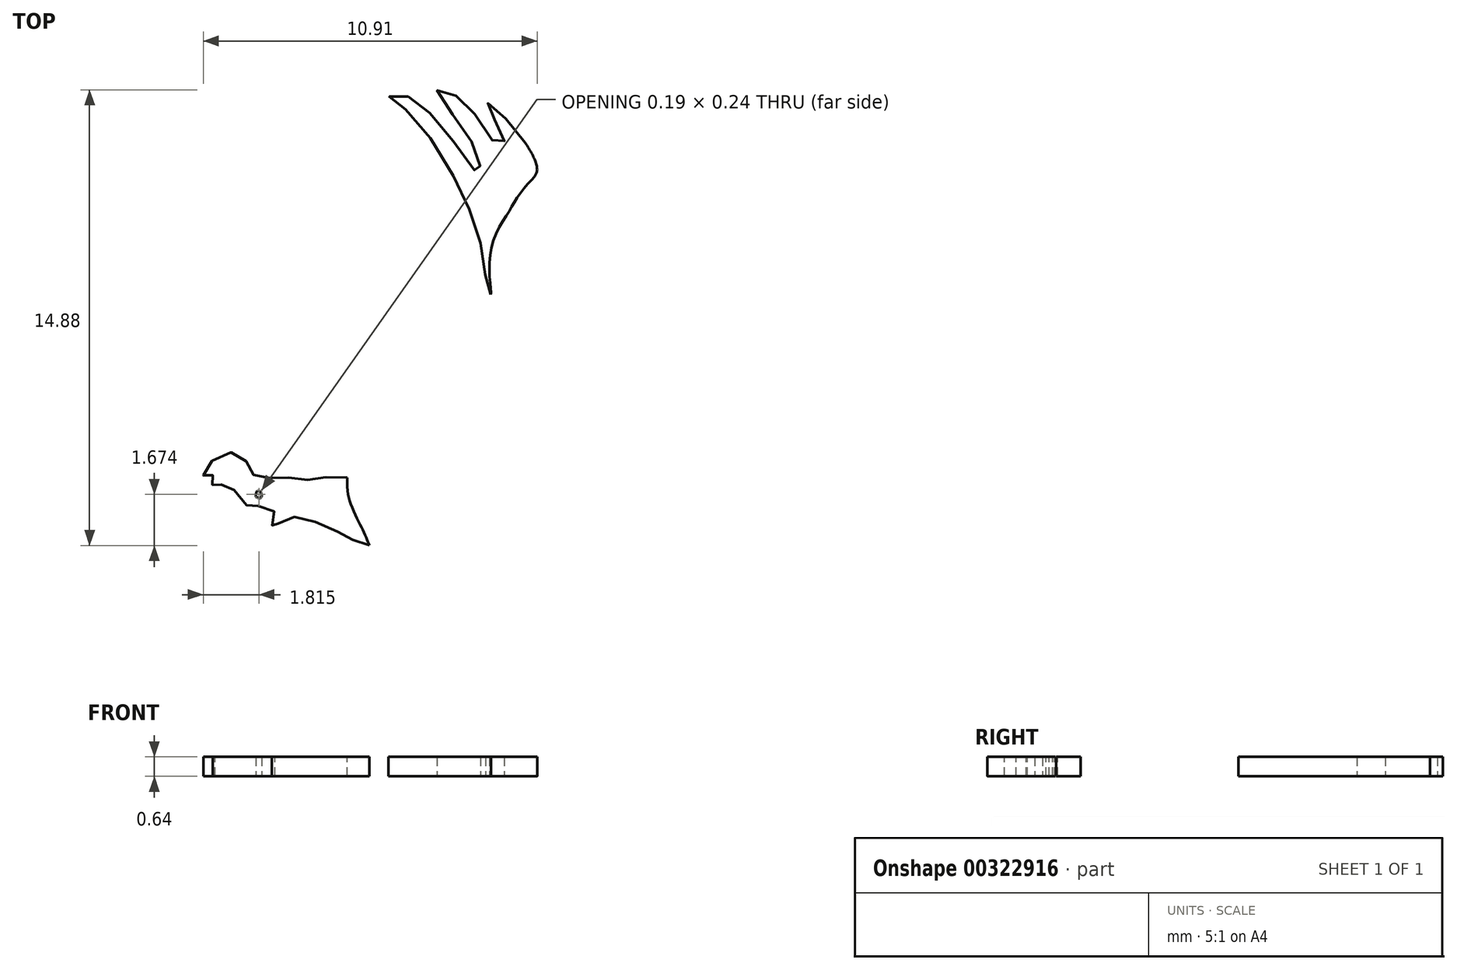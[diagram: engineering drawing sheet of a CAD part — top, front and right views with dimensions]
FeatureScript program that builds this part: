
annotation { "Feature Type Name" : "Feature", "Feature Type Description" : "" }
export const myFeature = defineFeature(function(context is Context, id is Id, definition is map)
    precondition{}
    {
        {
            var Q0;
            Q0=qCreatedBy(makeId("Top.planeOp"),FACE);
            var sketch = newSketch(context, id + "F0", { "sketchPlane" : qUnion([Q0])});
            skLineSegment(sketch, "E0", {"start": v(-2.65, -7.8) * mm, "end": v(0.66, -7.8) * mm});
            skLineSegment(sketch, "E1", {"start": v(0.66, -7.8) * mm, "end": v(-0.1, -6.67) * mm});
            skLineSegment(sketch, "E2", {"start": v(-0.1, -6.67) * mm, "end": v(-3.36, -6.67) * mm});
            skLineSegment(sketch, "E3", {"start": v(-3.36, -6.67) * mm, "end": v(-2.65, -7.8) * mm});
            skLineSegment(sketch, "E4", {"start": v(4.6, -7.8) * mm, "end": v(7.37, -7.7) * mm});
            skLineSegment(sketch, "E5", {"start": v(7.37, -7.7) * mm, "end": v(6.5, -6.65) * mm});
            skLineSegment(sketch, "E6", {"start": v(6.5, -6.65) * mm, "end": v(3.6, -6.73) * mm});
            skLineSegment(sketch, "E7", {"start": v(3.6, -6.73) * mm, "end": v(4.6, -7.8) * mm});
            skFitSpline(sketch, "E8", {"points": [v(-7.27, -6.68) * mm, v(-7.08, -6.58) * mm, v(-6.94, -6.5) * mm, v(-6.73, -6.5) * mm, v(-6.69, -6.62) * mm, v(-6.5, -6.89) * mm, v(-6.2, -7.32) * mm, v(-6.03, -7.65) * mm, v(-6.02, -7.73) * mm, v(-6, -7.8) * mm, v(-6.35, -7.85) * mm, v(-6.98, -7.9) * mm, v(-7.9, -7.87) * mm, v(-8.38, -7.71) * mm, v(-8.62, -7.55) * mm, v(-8.68, -7.37) * mm, v(-8.61, -7.07) * mm, v(-8.44, -6.87) * mm, v(-7.98, -6.7) * mm, v(-7.53, -6.56) * mm, v(-7.4, -6.48) * mm, v(-7.36, -6.46) * mm, v(-7.32, -6.52) * mm, v(-7.3, -6.6) * mm, v(-7.27, -6.68) * mm]});
            skFitSpline(sketch, "E9", {"points": [v(-1.27, -6.52) * mm, v(-1.14, -6.29) * mm, v(-1.06, -6.05) * mm, v(-1.05, -5.83) * mm, v(-1.06, -5.78) * mm, v(-1.19, -5.86) * mm, v(-1.37, -6.07) * mm, v(-1.44, -6.33) * mm, v(-1.43, -6.42) * mm, v(-1.35, -6.5) * mm, v(-1.27, -6.52) * mm]});
            skFitSpline(sketch, "E10", {"points": [v(8, -5.7) * mm, v(8.08, -5.77) * mm, v(8.1, -5.98) * mm, v(7.99, -6.24) * mm, v(7.85, -6.36) * mm, v(7.79, -6.4) * mm, v(7.71, -6.31) * mm, v(7.7, -6.05) * mm, v(7.85, -5.82) * mm, v(8, -5.7) * mm]});
            skFitSpline(sketch, "E11", {"points": [v(-2.87, -2.94) * mm, v(-2.6, -2.91) * mm, v(-2.31, -2.71) * mm, v(-2.17, -2.46) * mm, v(-2.17, -2.41) * mm, v(-2.24, -2.33) * mm, v(-2.33, -2.3) * mm, v(-2.48, -2.4) * mm, v(-2.62, -2.58) * mm, v(-2.74, -2.76) * mm, v(-2.8, -2.86) * mm, v(-2.87, -2.94) * mm]});
            skFitSpline(sketch, "E12", {"points": [v(-3.18, 5.99) * mm, v(-3.22, 6.13) * mm, v(-3.35, 6.22) * mm, v(-3.54, 6.2) * mm, v(-3.64, 6.1) * mm, v(-3.64, 5.97) * mm, v(-3.5, 5.88) * mm, v(-3.27, 5.92) * mm, v(-3.2, 5.95) * mm, v(-3.18, 5.99) * mm]});
            skFitSpline(sketch, "E13", {"points": [v(-8.53, -0.56) * mm, v(-8.5, -0.45) * mm, v(-8.54, -0.37) * mm, v(-8.61, -0.32) * mm, v(-8.67, -0.37) * mm, v(-8.7, -0.46) * mm, v(-8.7, -0.51) * mm, v(-8.63, -0.57) * mm, v(-8.53, -0.56) * mm]});
            skFitSpline(sketch, "E14", {"points": [v(-5.7, 0.1) * mm, v(-5.7, -0.28) * mm, v(-5.62, -0.68) * mm, v(-5.41, -1.2) * mm, v(-5.23, -1.54) * mm, v(-5.1, -1.8) * mm, v(-5.03, -2) * mm, v(-4.99, -2.11) * mm, v(-5.11, -2.1) * mm, v(-5.51, -1.95) * mm, v(-5.6, -1.88) * mm, v(-5.87, -1.74) * mm, v(-6.4, -1.5) * mm, v(-6.88, -1.3) * mm, v(-7.3, -1.2) * mm, v(-7.67, -1.22) * mm, v(-7.92, -1.35) * mm, v(-8.05, -1.5) * mm, v(-8.11, -1.57) * mm, v(-8.14, -1.55) * mm, v(-8.16, -1.39) * mm, v(-8.09, -1.23) * mm, v(-8.1, -1) * mm, v(-8.27, -0.87) * mm, v(-8.63, -0.82) * mm, v(-8.84, -0.84) * mm, v(-8.94, -0.86) * mm, v(-9.03, -0.77) * mm, v(-9.27, -0.47) * mm, v(-9.48, -0.2) * mm, v(-9.63, -0.1) * mm, v(-9.85, -0.14) * mm, v(-10, -0.2) * mm, v(-10.07, -0.2) * mm, v(-10.1, -0.17) * mm, v(-10.08, -0.07) * mm, v(-10.03, 0.04) * mm, v(-10.06, 0.13) * mm, v(-10.13, 0.18) * mm, v(-10.23, 0.17) * mm, v(-10.35, 0.16) * mm, v(-10.4, 0.16) * mm, v(-10.33, 0.39) * mm, v(-10.17, 0.6) * mm, v(-9.85, 0.84) * mm, v(-9.44, 0.92) * mm, v(-9.13, 0.8) * mm, v(-8.97, 0.55) * mm, v(-8.87, 0.31) * mm, v(-8.76, 0.18) * mm, v(-8.6, 0.1) * mm, v(-8.3, 0.08) * mm, v(-7.91, 0.11) * mm, v(-7.6, 0.1) * mm, v(-7.2, 0) * mm, v(-6.9, 0.05) * mm, v(-6.58, 0.1) * mm, v(-6.17, 0.12) * mm, v(-5.7, 0.1) * mm, v(-5.7, 0.1) * mm]});
            skFitSpline(sketch, "E15", {"points": [v(-4.83, -5.9) * mm, v(-4.95, -5.73) * mm, v(-5.1, -5.65) * mm, v(-5.3, -5.65) * mm, v(-5.54, -5.76) * mm, v(-5.79, -5.98) * mm, v(-5.92, -6.16) * mm, v(-5.97, -6.24) * mm, v(-5.98, -6.28) * mm, v(-5.55, -6.31) * mm, v(-4.77, -6.33) * mm, v(-3.69, -6.33) * mm, v(-2.83, -6.32) * mm, v(-2.13, -6.33) * mm, v(-2, -6.32) * mm, v(-1.95, -6.3) * mm, v(-1.86, -6.05) * mm, v(-1.85, -6) * mm, v(-1.56, -5.66) * mm, v(-0.98, -5.46) * mm, v(-0.5, -5.44) * mm, v(-0.27, -5.46) * mm, v(-0.2, -5.42) * mm, v(0.38, -4.7) * mm, v(0.7, -4.3) * mm, v(0.85, -4.1) * mm, v(0.85, -3.83) * mm, v(0.82, -3.33) * mm, v(0.72, -2.88) * mm, v(0.67, -2.31) * mm, v(0.67, -2.17) * mm, v(0.6, -2.14) * mm, v(0.54, -2.07) * mm, v(0.45, -2.1) * mm, v(0.04, -2.3) * mm, v(-0.47, -2.54) * mm, v(-1.24, -2.9) * mm, v(-1.8, -3.06) * mm, v(-2.52, -3.16) * mm, v(-2.97, -3.26) * mm, v(-3.3, -3.4) * mm, v(-3.71, -3.86) * mm, v(-4, -4.26) * mm, v(-4.05, -4.32) * mm, v(-4.4, -4.69) * mm, v(-4.59, -4.91) * mm, v(-4.77, -5.3) * mm, v(-4.81, -5.63) * mm, v(-4.82, -5.85) * mm, v(-4.83, -5.9) * mm]});
            skFitSpline(sketch, "E16", {"points": [v(8.37, -5.29) * mm, v(8.16, -4.77) * mm, v(7.88, -4.27) * mm, v(7.55, -3.92) * mm, v(7.26, -3.8) * mm, v(6.8, -3.76) * mm, v(6.22, -3.8) * mm, v(5.74, -3.85) * mm, v(5.47, -3.84) * mm, v(5.3, -3.83) * mm, v(5.2, -3.83) * mm, v(4.99, -3.42) * mm, v(4.73, -2.73) * mm, v(4.57, -2.26) * mm, v(4.38, -1.86) * mm, v(4.22, -1.6) * mm, v(4.16, -1.51) * mm, v(3.83, -1.45) * mm, v(3.42, -1.35) * mm, v(3.05, -1.34) * mm, v(2.72, -1.62) * mm, v(2.49, -2.08) * mm, v(2.43, -2.92) * mm, v(2.45, -4) * mm, v(2.44, -4.4) * mm, v(2.44, -4.48) * mm, v(2.2, -4.6) * mm, v(1.84, -4.83) * mm, v(1.04, -5.37) * mm, v(0.61, -5.65) * mm, v(0.32, -5.9) * mm, v(0.08, -6.2) * mm, v(0.04, -6.27) * mm, v(0.38, -6.3) * mm, v(2.63, -6.34) * mm, v(4.92, -6.32) * mm, v(6.38, -6.3) * mm, v(6.85, -6.28) * mm, v(7, -6.28) * mm, v(7.04, -6.18) * mm, v(7.24, -5.82) * mm, v(7.73, -5.45) * mm, v(8.14, -5.34) * mm, v(8.4, -5.33) * mm, v(8.37, -5.29) * mm]});
            skFitSpline(sketch, "E17", {"points": [v(-1.02, 6.22) * mm, v(-1.06, 6.93) * mm, v(-0.88, 7.98) * mm, v(-0.45, 8.75) * mm, v(-0.18, 9.2) * mm, v(0.21, 9.7) * mm, v(0.48, 10.05) * mm, v(0.44, 10.42) * mm, v(0.1, 11.04) * mm, v(-0.33, 11.6) * mm, v(-0.67, 11.98) * mm, v(-0.98, 12.24) * mm, v(-1.17, 12.34) * mm, v(-1.18, 12.24) * mm, v(-0.9, 11.79) * mm, v(-0.71, 11.5) * mm, v(-0.57, 11.08) * mm, v(-0.62, 10.88) * mm, v(-0.8, 10.94) * mm, v(-1.24, 11.48) * mm, v(-1.57, 12) * mm, v(-1.87, 12.35) * mm, v(-2.27, 12.63) * mm, v(-2.63, 12.74) * mm, v(-2.77, 12.75) * mm, v(-2.66, 12.51) * mm, v(-2.2, 11.88) * mm, v(-1.75, 11.28) * mm, v(-1.43, 10.6) * mm, v(-1.37, 10.3) * mm, v(-1.36, 10.09) * mm, v(-1.36, 9.95) * mm, v(-1.7, 10.33) * mm, v(-2.21, 11.04) * mm, v(-2.84, 11.82) * mm, v(-3.35, 12.3) * mm, v(-3.71, 12.53) * mm, v(-3.76, 12.56) * mm, v(-4.17, 12.57) * mm, v(-4.34, 12.53) * mm, v(-4.36, 12.48) * mm, v(-4.08, 12.33) * mm, v(-3.39, 11.7) * mm, v(-2.77, 10.85) * mm, v(-2.08, 9.65) * mm, v(-1.71, 8.84) * mm, v(-1.42, 7.98) * mm, v(-1.25, 7.28) * mm, v(-1.2, 6.6) * mm, v(-1.17, 6.3) * mm, v(-1.03, 6.08) * mm, v(-1.02, 6.22) * mm]});
            skFitSpline(sketch, "E18", {"points": [v(-7.76, -6.35) * mm, v(-7.74, -6.2) * mm, v(-7.65, -5.96) * mm, v(-7.41, -5.68) * mm, v(-7.15, -5.53) * mm, v(-6.75, -5.42) * mm, v(-6.4, -5.39) * mm, v(-6.23, -5.4) * mm, v(-6.04, -5.12) * mm, v(-5.68, -4.5) * mm, v(-5.3, -3.77) * mm, v(-4.76, -2.73) * mm, v(-4.63, -2.49) * mm, v(-4.61, -2.45) * mm, v(-4.6, -2.43) * mm, v(-4.63, -2.33) * mm, v(-4.73, -2.1) * mm, v(-4.87, -1.8) * mm, v(-4.9, -1.72) * mm, v(-4.9, -1.51) * mm, v(-4.88, -1.26) * mm, v(-4.82, -0.87) * mm, v(-4.72, -0.49) * mm, v(-4.59, -0.09) * mm, v(-4.4, 0.34) * mm, v(-4.34, 0.49) * mm, v(-4.32, 0.52) * mm, v(-4.16, 0.66) * mm, v(-4.07, 0.8) * mm, v(-4.06, 0.95) * mm, v(-4.09, 1.04) * mm, v(-4.15, 1.03) * mm, v(-4.37, 0.9) * mm, v(-4.53, 0.75) * mm, v(-4.73, 0.45) * mm, v(-4.86, 0.17) * mm, v(-4.97, -0.22) * mm, v(-5.02, -0.63) * mm, v(-5.04, -0.96) * mm, v(-5.04, -1.1) * mm, v(-5.03, -1.12) * mm, v(-5.1, -1.05) * mm, v(-5.3, -0.68) * mm, v(-5.45, -0.18) * mm, v(-5.5, 0.17) * mm, v(-5.52, 0.6) * mm, v(-5.46, 1.1) * mm, v(-5.36, 1.5) * mm, v(-5.08, 2.18) * mm, v(-4.6, 2.97) * mm, v(-4.11, 3.6) * mm, v(-3.9, 3.83) * mm, v(-3.72, 3.93) * mm, v(-3.5, 4.12) * mm, v(-3.43, 4.24) * mm, v(-3.42, 4.33) * mm, v(-3.45, 4.43) * mm, v(-3.54, 4.47) * mm, v(-3.78, 4.4) * mm, v(-4.07, 4.17) * mm, v(-4.35, 3.98) * mm, v(-4.54, 3.9) * mm, v(-4.64, 3.86) * mm, v(-4.7, 3.86) * mm, v(-4.72, 3.86) * mm, v(-4.72, 3.92) * mm, v(-4.55, 4.11) * mm, v(-4.27, 4.3) * mm, v(-4.09, 4.48) * mm, v(-4.02, 4.65) * mm, v(-4, 4.73) * mm, v(-4.07, 4.74) * mm, v(-4.27, 4.77) * mm, v(-4.47, 4.73) * mm, v(-4.64, 4.64) * mm, v(-4.82, 4.45) * mm, v(-5, 4.2) * mm, v(-5.18, 3.92) * mm, v(-5.35, 3.7) * mm, v(-5.54, 3.54) * mm, v(-5.68, 3.47) * mm, v(-5.84, 3.47) * mm, v(-6.04, 3.45) * mm, v(-6.2, 3.4) * mm, v(-6.27, 3.32) * mm, v(-6.3, 3.28) * mm, v(-6.33, 3.28) * mm, v(-6.46, 3.4) * mm, v(-6.6, 3.57) * mm, v(-6.7, 3.78) * mm, v(-6.76, 3.9) * mm, v(-6.76, 3.92) * mm, v(-6.64, 3.94) * mm, v(-6.63, 3.94) * mm, v(-6.4, 4) * mm, v(-6.19, 4.04) * mm, v(-5.99, 4.06) * mm, v(-6, 3.98) * mm, v(-6.11, 3.88) * mm, v(-6.16, 3.83) * mm, v(-6.16, 3.78) * mm, v(-6.06, 3.73) * mm, v(-5.88, 3.68) * mm, v(-5.68, 3.72) * mm, v(-5.47, 3.85) * mm, v(-5.29, 4.04) * mm, v(-5.03, 4.37) * mm, v(-4.84, 4.6) * mm, v(-4.65, 4.8) * mm, v(-4.52, 4.92) * mm, v(-4.35, 5) * mm, v(-4.18, 5) * mm, v(-4.05, 4.98) * mm, v(-3.9, 4.91) * mm, v(-3.77, 4.82) * mm, v(-3.75, 4.8) * mm, v(-3.72, 4.78) * mm, v(-3.62, 4.9) * mm, v(-3.54, 5.03) * mm, v(-3.53, 5.2) * mm, v(-3.55, 5.3) * mm, v(-3.66, 5.34) * mm, v(-3.98, 5.4) * mm, v(-4.28, 5.42) * mm, v(-4.64, 5.41) * mm, v(-4.95, 5.33) * mm, v(-5.15, 5.19) * mm, v(-5.26, 4.96) * mm, v(-5.27, 4.8) * mm, v(-5.26, 4.73) * mm, v(-5.32, 4.8) * mm, v(-5.41, 5) * mm, v(-5.46, 5.27) * mm, v(-5.45, 5.5) * mm, v(-5.39, 5.67) * mm, v(-5.38, 5.7) * mm, v(-5.24, 5.84) * mm, v(-5.06, 5.92) * mm, v(-4.8, 5.92) * mm, v(-4.59, 5.92) * mm, v(-4.39, 5.98) * mm, v(-4.16, 6.2) * mm, v(-4.03, 6.36) * mm, v(-3.92, 6.43) * mm, v(-3.67, 6.49) * mm, v(-3.37, 6.52) * mm, v(-2.98, 6.52) * mm, v(-2.67, 6.5) * mm, v(-2.37, 6.44) * mm, v(-2.13, 6.36) * mm, v(-1.87, 6.23) * mm, v(-1.76, 6.14) * mm, v(-1.65, 5.98) * mm, v(-1.57, 5.73) * mm, v(-1.5, 5.5) * mm, v(-1.45, 5.22) * mm, v(-1.4, 4.86) * mm, v(-1.36, 4.55) * mm, v(-1.33, 4.21) * mm, v(-1.32, 3.87) * mm, v(-1.31, 3.52) * mm, v(-1.32, 3.23) * mm, v(-1.36, 2.79) * mm, v(-1.42, 2.42) * mm, v(-1.48, 2.2) * mm, v(-1.54, 2.02) * mm, v(-1.53, 1.94) * mm, v(-1.46, 1.9) * mm, v(-1.42, 1.88) * mm, v(-1.37, 1.87) * mm, v(-1.27, 1.85) * mm, v(-1.2, 1.82) * mm, v(-1.19, 1.78) * mm, v(-1.22, 1.62) * mm, v(-1.35, 1.43) * mm, v(-1.5, 1.27) * mm, v(-1.57, 1.14) * mm, v(-1.57, 0.98) * mm, v(-1.56, 0.93) * mm, v(-1.47, 0.93) * mm, v(-1.3, 0.98) * mm, v(-1.19, 1.1) * mm, v(-1.07, 1.34) * mm, v(-1, 1.5) * mm, v(-0.93, 1.6) * mm, v(-0.87, 1.65) * mm, v(-0.84, 1.8) * mm, v(-0.8, 2.02) * mm, v(-0.77, 2.27) * mm, v(-0.74, 2.52) * mm, v(-0.72, 2.78) * mm, v(-0.7, 2.98) * mm, v(-0.7, 3.27) * mm, v(-0.68, 3.58) * mm, v(-0.68, 4) * mm, v(-0.68, 4.57) * mm, v(-0.68, 5.07) * mm, v(-0.68, 5.77) * mm, v(-0.65, 6.47) * mm, v(-0.62, 6.91) * mm, v(-0.56, 7.35) * mm, v(-0.46, 7.71) * mm, v(-0.34, 8) * mm, v(-0.1, 8.44) * mm, v(0.12, 8.76) * mm, v(0.41, 9.14) * mm, v(0.85, 9.72) * mm, v(1.15, 10.15) * mm, v(1.4, 10.57) * mm, v(1.65, 10.99) * mm, v(1.94, 11.55) * mm, v(2.23, 12.18) * mm, v(2.5, 12.81) * mm, v(2.62, 13.11) * mm, v(2.67, 13.2) * mm, v(2.78, 13.1) * mm, v(2.89, 12.97) * mm, v(3.03, 12.66) * mm, v(3.04, 12.29) * mm, v(2.99, 12) * mm, v(2.86, 11.6) * mm, v(2.7, 11.19) * mm, v(2.57, 10.77) * mm, v(2.55, 10.65) * mm, v(2.53, 10.54) * mm, v(2.64, 10.52) * mm, v(2.8, 10.56) * mm, v(2.89, 10.66) * mm, v(3, 10.87) * mm, v(3.08, 11) * mm, v(3.15, 11.05) * mm, v(3.19, 11.07) * mm, v(3.26, 11.16) * mm, v(3.38, 11.32) * mm, v(3.5, 11.48) * mm, v(3.7, 11.73) * mm, v(3.95, 12.02) * mm, v(4.2, 12.33) * mm, v(4.36, 12.55) * mm, v(4.47, 12.72) * mm, v(4.6, 12.9) * mm, v(4.71, 13.14) * mm, v(4.77, 13.27) * mm, v(4.79, 13.29) * mm, v(4.83, 13.26) * mm, v(5.01, 13.09) * mm, v(5.13, 12.91) * mm, v(5.2, 12.8) * mm, v(5.24, 12.75) * mm, v(5.24, 12.73) * mm, v(5.15, 12.51) * mm, v(4.98, 12.11) * mm, v(4.87, 11.9) * mm, v(4.62, 11.47) * mm, v(4.32, 11.1) * mm, v(4.18, 10.95) * mm, v(4.16, 10.93) * mm, v(4.15, 10.9) * mm, v(4.1, 10.72) * mm, v(3.97, 10.49) * mm, v(3.72, 10.23) * mm, v(3.6, 10.1) * mm, v(3.48, 9.88) * mm, v(3.46, 9.74) * mm, v(3.47, 9.63) * mm, v(3.47, 9.58) * mm, v(3.61, 9.64) * mm, v(3.89, 9.8) * mm, v(4.23, 10.04) * mm, v(4.7, 10.45) * mm, v(5.15, 10.9) * mm, v(5.52, 11.28) * mm, v(5.84, 11.6) * mm, v(6.07, 11.82) * mm, v(6.26, 11.98) * mm, v(6.35, 12.06) * mm, v(6.38, 12.06) * mm, v(6.38, 11.85) * mm, v(6.38, 11.5) * mm, v(6.41, 11.33) * mm, v(6.4, 11.26) * mm, v(6.14, 10.9) * mm, v(5.84, 10.52) * mm, v(5.53, 10.16) * mm, v(5.26, 9.85) * mm, v(4.89, 9.45) * mm, v(4.57, 9.13) * mm, v(4.39, 8.95) * mm, v(4.25, 8.83) * mm, v(4.07, 8.74) * mm, v(3.91, 8.6) * mm, v(3.84, 8.46) * mm, v(3.84, 8.34) * mm, v(3.9, 8.28) * mm, v(3.93, 8.22) * mm, v(3.94, 8.22) * mm, v(4.3, 8.34) * mm, v(4.8, 8.56) * mm, v(5.14, 8.76) * mm, v(5.5, 8.96) * mm, v(5.81, 9.13) * mm, v(6.01, 9.25) * mm, v(6.06, 9.26) * mm, v(6.03, 9.09) * mm, v(5.97, 8.8) * mm, v(5.86, 8.56) * mm, v(5.82, 8.47) * mm, v(5.7, 8.3) * mm, v(5.46, 8.05) * mm, v(5.16, 7.81) * mm, v(4.96, 7.69) * mm, v(4.67, 7.53) * mm, v(4.28, 7.33) * mm, v(3.93, 7.12) * mm, v(3.72, 7.05) * mm, v(3.43, 6.86) * mm, v(3.16, 6.65) * mm, v(3.05, 6.53) * mm, v(3, 6.46) * mm, v(3.01, 6.42) * mm, v(3.24, 6.31) * mm, v(3.64, 6.32) * mm, v(4.06, 6.4) * mm, v(4.42, 6.5) * mm, v(4.75, 6.55) * mm, v(4.95, 6.55) * mm, v(4.97, 6.55) * mm, v(4.95, 6.4) * mm, v(4.84, 6.1) * mm, v(4.78, 5.96) * mm, v(4.7, 5.76) * mm, v(4.7, 5.7) * mm, v(4.71, 5.68) * mm, v(4.64, 5.64) * mm, v(4.28, 5.47) * mm, v(4.01, 5.37) * mm, v(3.63, 5.23) * mm, v(3.14, 5.09) * mm, v(2.77, 5.01) * mm, v(2.77, 5.01) * mm, v(2.46, 4.96) * mm, v(2.44, 4.95) * mm, v(2.44, 4.86) * mm, v(2.6, 4.75) * mm, v(2.65, 4.7) * mm, v(2.67, 4.63) * mm, v(2.67, 4.56) * mm, v(2.67, 4.55) * mm, v(2.88, 4.57) * mm, v(3.18, 4.6) * mm, v(3.56, 4.61) * mm, v(3.7, 4.6) * mm, v(3.74, 4.6) * mm, v(3.75, 4.58) * mm, v(3.76, 4.44) * mm, v(3.76, 4.05) * mm, v(3.75, 3.78) * mm, v(3.75, 3.72) * mm, v(3.6, 3.7) * mm, v(3.17, 3.68) * mm, v(2.66, 3.7) * mm, v(2.38, 3.69) * mm, v(2.35, 3.68) * mm, v(2.25, 3.58) * mm, v(2.21, 3.38) * mm, v(2.23, 3.28) * mm, v(2.25, 3.25) * mm, v(2.25, 3.24) * mm, v(2.5, 3.2) * mm, v(2.52, 3.2) * mm, v(3.04, 3.22) * mm, v(3.36, 3.23) * mm, v(3.63, 3.21) * mm, v(3.72, 3.2) * mm, v(3.75, 3.2) * mm, v(3.76, 3.15) * mm, v(3.77, 2.86) * mm, v(3.75, 2.55) * mm, v(3.72, 2.34) * mm, v(3.7, 2.26) * mm, v(3.7, 2.23) * mm, v(3.68, 2.22) * mm, v(3.44, 2.22) * mm, v(3.15, 2.23) * mm, v(2.8, 2.25) * mm, v(2.4, 2.23) * mm, v(2.27, 2.2) * mm, v(2.18, 2.16) * mm, v(2.17, 2.13) * mm, v(2.16, 1.9) * mm, v(2.16, 1.87) * mm, v(2.25, 1.8) * mm, v(2.38, 1.76) * mm, v(2.57, 1.76) * mm, v(2.72, 1.78) * mm, v(2.96, 1.78) * mm, v(3.3, 1.72) * mm, v(3.49, 1.68) * mm, v(3.78, 1.58) * mm, v(4.08, 1.46) * mm, v(4.4, 1.3) * mm, v(4.53, 1.22) * mm, v(4.57, 1.2) * mm, v(4.64, 1.26) * mm, v(4.84, 1.45) * mm, v(4.95, 1.54) * mm, v(5.11, 1.6) * mm, v(5.29, 1.6) * mm, v(5.47, 1.59) * mm, v(5.48, 1.59) * mm, v(5.7, 1.55) * mm, v(5.93, 1.49) * mm, v(6.1, 1.43) * mm, v(6.33, 1.36) * mm, v(6.34, 1.36) * mm, v(6.73, 1.24) * mm, v(6.98, 1.2) * mm, v(7.12, 1.19) * mm, v(7.35, 1.25) * mm, v(7.47, 1.4) * mm, v(7.53, 1.55) * mm, v(7.55, 1.77) * mm, v(7.5, 1.96) * mm, v(7.38, 2.2) * mm, v(7.16, 2.46) * mm, v(7, 2.62) * mm, v(6.79, 2.83) * mm, v(6.66, 2.94) * mm, v(6.44, 3.15) * mm, v(6.42, 3.16) * mm, v(6.28, 3.29) * mm, v(6.1, 3.5) * mm, v(5.86, 3.8) * mm, v(5.76, 4.05) * mm, v(5.72, 4.32) * mm, v(5.74, 4.51) * mm, v(5.79, 4.7) * mm, v(5.9, 4.9) * mm, v(6.01, 5.06) * mm, v(6.18, 5.14) * mm, v(6.43, 5.23) * mm, v(6.62, 5.26) * mm, v(6.93, 5.25) * mm, v(6.95, 5.25) * mm, v(7.07, 5.22) * mm, v(7.32, 5.11) * mm, v(7.5, 5) * mm, v(7.67, 4.85) * mm, v(7.84, 4.67) * mm, v(7.99, 4.47) * mm, v(8.1, 4.27) * mm, v(8.2, 4.06) * mm, v(8.3, 3.82) * mm, v(8.38, 3.5) * mm, v(8.4, 3.34) * mm, v(8.4, 3.28) * mm, v(8.31, 3.4) * mm, v(8.3, 3.42) * mm, v(8.15, 3.63) * mm, v(8, 3.82) * mm, v(7.8, 4.03) * mm, v(7.8, 4.04) * mm, v(7.64, 4.14) * mm, v(7.3, 4.29) * mm, v(7.15, 4.31) * mm, v(7.1, 4.32) * mm, v(7.14, 4.36) * mm, v(7.28, 4.55) * mm, v(7.3, 4.62) * mm, v(7.31, 4.69) * mm, v(7.3, 4.71) * mm, v(7.27, 4.81) * mm, v(7.15, 4.92) * mm, v(6.95, 5) * mm, v(6.94, 5) * mm, v(6.8, 5.03) * mm, v(6.58, 5.03) * mm, v(6.38, 5) * mm, v(6.24, 4.93) * mm, v(6.16, 4.89) * mm, v(6.04, 4.76) * mm, v(5.98, 4.62) * mm, v(5.98, 4.4) * mm, v(6.04, 4.2) * mm, v(6.11, 4.02) * mm, v(6.23, 3.82) * mm, v(6.46, 3.53) * mm, v(6.78, 3.23) * mm, v(7.08, 2.98) * mm, v(7.44, 2.67) * mm, v(7.73, 2.37) * mm, v(7.87, 2.14) * mm, v(7.97, 1.85) * mm, v(8, 1.52) * mm, v(7.95, 1.24) * mm, v(7.87, 1.01) * mm, v(7.79, 0.84) * mm, v(7.65, 0.75) * mm, v(7.43, 0.67) * mm, v(7.24, 0.65) * mm, v(7, 0.67) * mm, v(6.75, 0.73) * mm, v(6.24, 0.87) * mm, v(5.96, 0.92) * mm, v(5.64, 0.91) * mm, v(5.49, 0.86) * mm, v(5.34, 0.78) * mm, v(5.3, 0.75) * mm, v(5.3, 0.74) * mm, v(5.3, 0.66) * mm, v(5.43, 0.4) * mm, v(5.55, 0.24) * mm, v(5.73, 0.03) * mm, v(5.94, -0.18) * mm, v(6.12, -0.39) * mm, v(6.23, -0.55) * mm, v(6.3, -0.7) * mm, v(6.39, -0.88) * mm, v(6.5, -1.14) * mm, v(6.57, -1.33) * mm, v(6.67, -1.53) * mm, v(6.75, -1.64) * mm, v(6.81, -1.72) * mm, v(6.83, -1.73) * mm, v(6.84, -1.87) * mm, v(6.9, -2.14) * mm, v(7, -2.37) * mm, v(7.04, -2.46) * mm, v(7.05, -2.5) * mm, v(7.08, -2.51) * mm, v(7.3, -2.52) * mm, v(7.67, -2.51) * mm, v(7.91, -2.5) * mm, v(8.12, -2.52) * mm, v(8.3, -2.55) * mm, v(8.36, -2.56) * mm, v(8.37, -2.56) * mm, v(8.39, -2.65) * mm, v(8.43, -2.82) * mm, v(8.5, -3.07) * mm, v(8.6, -3.31) * mm, v(8.7, -3.61) * mm, v(8.85, -3.98) * mm, v(8.94, -4.22) * mm, v(9.02, -4.44) * mm, v(9.12, -4.7) * mm, v(9.2, -4.94) * mm, v(9.23, -5.12) * mm, v(9.26, -5.35) * mm, v(9.26, -5.64) * mm, v(9.2, -5.88) * mm, v(9.1, -6.13) * mm, v(9.01, -6.25) * mm, v(8.97, -6.3) * mm, v(8.96, -6.32) * mm, v(8.98, -6.37) * mm, v(9.05, -6.44) * mm, v(9.19, -6.5) * mm, v(9.28, -6.55) * mm, v(9.35, -6.63) * mm, v(9.4, -6.74) * mm, v(9.43, -6.9) * mm, v(9.41, -7.16) * mm, v(9.38, -7.32) * mm, v(9.3, -7.6) * mm, v(9.2, -7.86) * mm, v(9.2, -8) * mm, v(9.2, -8.07) * mm, v(9.2, -8.1) * mm, v(9.05, -8.09) * mm, v(8.54, -8.09) * mm, v(8.05, -8.08) * mm, v(7.54, -8.09) * mm, v(6.78, -8.08) * mm, v(5.98, -8.08) * mm, v(5.17, -8.08) * mm, v(4.38, -8.08) * mm, v(3.55, -8.08) * mm, v(2.73, -8.08) * mm, v(1.88, -8.1) * mm, v(1.08, -8.1) * mm, v(0.28, -8.09) * mm, v(-0.5, -8.09) * mm, v(-1.31, -8.09) * mm, v(-2.1, -8.1) * mm, v(-2.87, -8.1) * mm, v(-3.65, -8.1) * mm, v(-4.39, -8.1) * mm, v(-5.18, -8.1) * mm, v(-5.96, -8.1) * mm, v(-6.75, -8.1) * mm, v(-7.53, -8.1) * mm, v(-8.33, -8.11) * mm, v(-8.48, -8.11) * mm, v(-8.5, -8.1) * mm, v(-8.58, -8.04) * mm, v(-8.72, -7.9) * mm, v(-8.81, -7.72) * mm, v(-8.9, -7.46) * mm, v(-8.92, -7.3) * mm, v(-8.9, -7.1) * mm, v(-8.8, -6.82) * mm, v(-8.6, -6.57) * mm, v(-8.47, -6.48) * mm, v(-8.29, -6.4) * mm, v(-8.28, -6.4) * mm, v(-8.16, -6.36) * mm, v(-7.96, -6.35) * mm, v(-7.83, -6.35) * mm, v(-7.78, -6.36) * mm, v(-7.77, -6.35) * mm, v(-7.76, -6.35) * mm]});
            skArc(sketch, "E19", {"start": v(-5.7, 0.1) * mm, "mid": v(-5.6, 0.12) * mm, "end": v(-5.5, 0.17) * mm});
            skArc(sketch, "E20", {"start": v(-4.63, -2.33) * mm, "mid": v(-4.77, -2.15) * mm, "end": v(-4.99, -2.11) * mm});
            skArc(sketch, "E21", {"start": v(-0.68, 5.07) * mm, "mid": v(-0.77, 5.6) * mm, "end": v(-1.03, 6.08) * mm});
            skArc(sketch, "E22", {"start": v(0.48, 10.05) * mm, "mid": v(0.4, 9.6) * mm, "end": v(0.41, 9.14) * mm});
            skArc(sketch, "E23", {"start": v(1.65, 10.99) * mm, "mid": v(0.9, 11.92) * mm, "end": v(0.1, 11.04) * mm});
            skCircle(sketch, "E24", {"center": v(0.88, 11.14) * mm, "radius": 0.57 * mm});
            skSolve(sketch);
        }
        {
            var Q0;
            Q0=makeQuery(id+"F0.imprint","IMPRINT",FACE,{"disambiguationData":[TD([[makeQuery(id+"F0.imprint","IMPRINT",EDGE,{"derivedFrom":sQuery(id+"F0.wireOp",EDGE,"E17")}),1.0]])]});
            var Q1;
            Q1=makeQuery(id+"F0.imprint","IMPRINT",FACE,{"disambiguationData":[TD([[makeQuery(id+"F0.imprint","IMPRINT",EDGE,{"derivedFrom":sQuery(id+"F0.wireOp",EDGE,"E0")}),-1.0]])]});
            var Q2;
            Q2=makeQuery(id+"F0.imprint","IMPRINT",FACE,{"disambiguationData":[TD([[makeQuery(id+"F0.imprint","IMPRINT",EDGE,{"derivedFrom":sQuery(id+"F0.wireOp",EDGE,"E13")}),-1.0]])]});
            var Q3;
            {var subQ3=sQuery(id+"F0.wireOp",EDGE,"E22");Q3=makeQuery(id+"F0.imprint","IMPRINT",FACE,{"disambiguationData":[TD([[makeQuery(id+"F0.imprint","IMPRINT",EDGE,{"derivedFrom":subQ3}),-1.0]])]});}
            var Q4;
            {var subQ0=sQuery(id+"F0.wireOp",EDGE,"E19");Q4=makeQuery(id+"F0.imprint","IMPRINT",FACE,{"disambiguationData":[TD([[makeQuery(id+"F0.imprint","IMPRINT",EDGE,{"derivedFrom":subQ0}),-1.0]])]});}
            var Q5;
            {var subQ1=sQuery(id+"F0.wireOp",EDGE,"E22");Q5=makeQuery(id+"F0.imprint","IMPRINT",FACE,{"disambiguationData":[TD([[makeQuery(id+"F0.imprint","IMPRINT",EDGE,{"derivedFrom":subQ1}),1.0]])]});}
            extrude(context, id + "F1", {"entities" : qUnion([Q0, Q1, Q2, Q3, Q4, Q5]), "depth" : 0.64 * mm});
        }
    });
